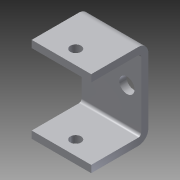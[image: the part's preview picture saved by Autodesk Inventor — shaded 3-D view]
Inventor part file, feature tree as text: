
AUTODESK INVENTOR PART (.ipt)
format: ipt  version: 2013 (Build 170138000, 138)  size: 130,048 bytes
history: native  units: in
note: dims shown in document units (in); Inventor stores cm internally (conversion verified against a paired STEP export)
features: sheet_metal_op x4, sketch x4, other x3, reference x2, extrude x1
ambient origin geometry x8: Origin, YZ Plane, XZ Plane, XY Plane, X Axis, Y Axis, Z Axis, Center Point
bodies: Solid1 (feature_tree)
feature tree (14):
  sheet_metal_op  "Face1"
  sheet_metal_op  "Flange1"
  extrude  "Extrusion1"  Depth=1.15in
  sketch  "Sketch1"  dims[d4=0.5788in d5=1.15in]
  other  "Plate1"
  sketch  "Sketch2"  dims[d6=0.125in]
  other  "Plate2"
  sheet_metal_op  "Bend1"
  sheet_metal_op  "Corner1"
  sketch  "Sketch3"  dims[d7=0.125in]
  sketch  "Sketch5"  dims[d8=0.0625in d9=0.25in d10=0.125in d11=1.0in d12=90.0deg d13=0.05in d14=0.5in d15=0.125in d16=0.125in d17=0.25in d18=0.1875in d19=2999.0in d20=0.0in d21=0.575in d22=0.125in d23=0.0in]
  reference  "Reference1"
  reference  "Reference2"
  other  "Cut1"
